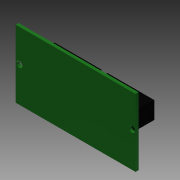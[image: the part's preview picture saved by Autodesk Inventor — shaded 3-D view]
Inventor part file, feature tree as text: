
AUTODESK INVENTOR PART (.ipt)
format: ipt  version: 2015 (Build 190159000, 159)  size: 104,448 bytes
history: native  units: mm
features: sketch x2, extrude x2
ambient origin geometry x8: Origin, YZ Plane, XZ Plane, XY Plane, X Axis, Y Axis, Z Axis, Center Point
bodies: Solid1 (feature_tree)
feature tree (4):
  sketch  "Sketch1"  dims[d0=69.215mm d1=38.989mm]
  extrude  "Extrusion1"  Depth=38.989mm
  extrude  "Extrusion2"  Depth=16.58mm
  sketch  "Sketch2"  dims[d2=3.5mm d3=2.172mm d4=20.216mm d5=27.0mm d6=10.0mm d14=1.7mm d15=0.0mm d16=16.58mm d17=0.0mm d18=64.884mm]
